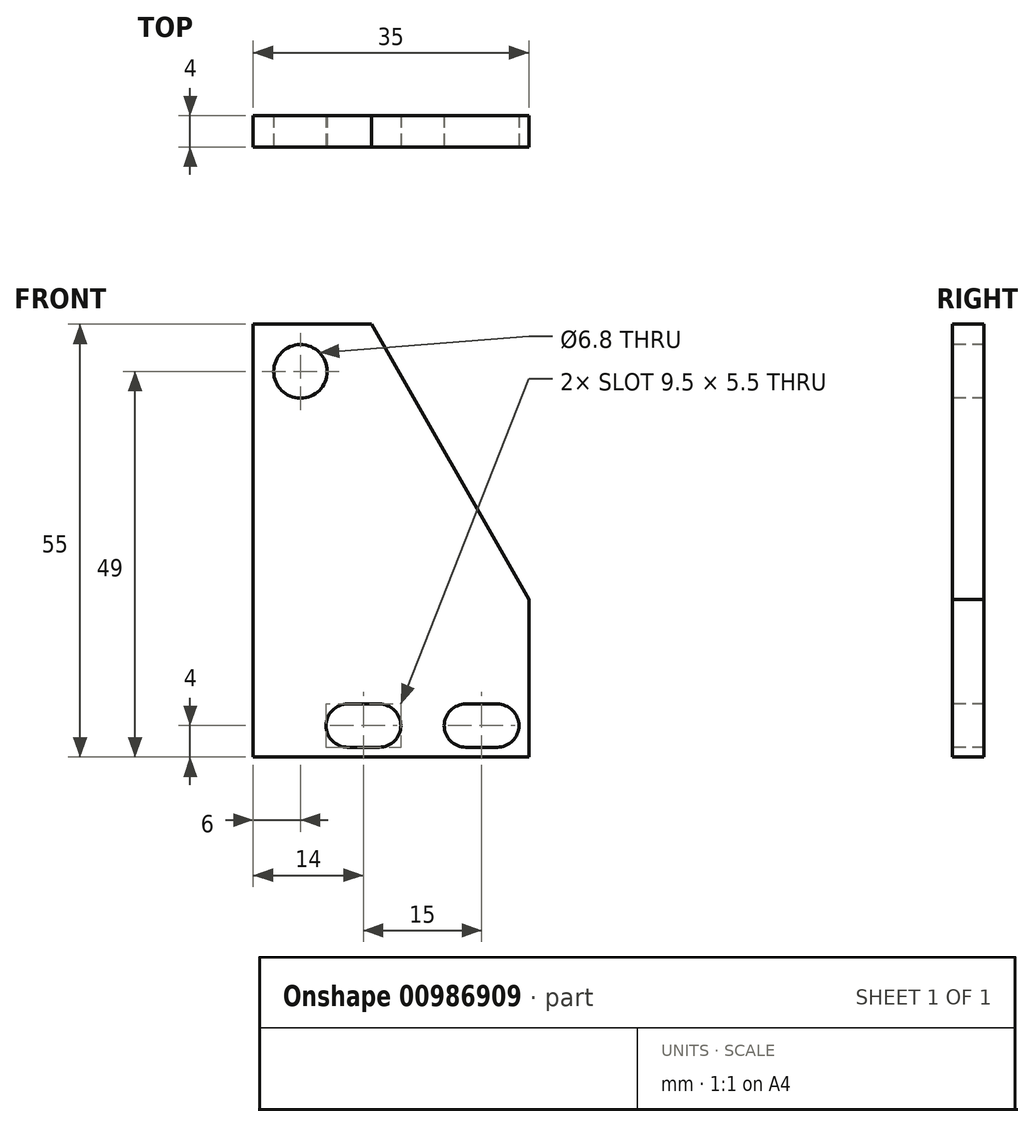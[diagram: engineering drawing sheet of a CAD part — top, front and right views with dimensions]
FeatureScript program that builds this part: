
annotation { "Feature Type Name" : "Feature", "Feature Type Description" : "" }
export const myFeature = defineFeature(function(context is Context, id is Id, definition is map)
    precondition{}
    {
        {
            var Q0;
            Q0=qCreatedBy(makeId("Front.planeOp"),FACE);
            var sketch = newSketch(context, id + "F0", { "sketchPlane" : qUnion([Q0])});
            skLineSegment(sketch, "E0", {"start": v(0, 0) * mm, "end": v(35, 0) * mm});
            skLineSegment(sketch, "E1", {"start": v(35, 0) * mm, "end": v(35, 20) * mm});
            skLineSegment(sketch, "E2", {"start": v(35, 20) * mm, "end": v(15, 55) * mm});
            skLineSegment(sketch, "E3", {"start": v(15, 55) * mm, "end": v(0, 55) * mm});
            skLineSegment(sketch, "E4", {"start": v(0, 55) * mm, "end": v(0, 0) * mm});
            skSolve(sketch);
        }
        {
            var Q0;
            Q0=makeQuery(id+"F0.imprint","IMPRINT",FACE,{"disambiguationData":[TD([[makeQuery(id+"F0.imprint","IMPRINT",EDGE,{"derivedFrom":sQuery(id+"F0.wireOp",EDGE,"E0")}),1.0]])]});
            extrude(context, id + "F1", {"entities" : qUnion([Q0]), "depth" : 4 * mm, "offsetDistance" : 25 * mm});
        }
        {
            var Q0;
            Q0=makeQuery(id+"F1.opExtrude","CAP_FACE",FACE,{"disambiguationData":[OSD([sQuery(id+"F0.wireOp",EDGE,"E0"),sQuery(id+"F0.wireOp",EDGE,"E1"),sQuery(id+"F0.wireOp",EDGE,"E2"),sQuery(id+"F0.wireOp",EDGE,"E3"),sQuery(id+"F0.wireOp",EDGE,"E4")])],"isStart":false});
            var sketch = newSketch(context, id + "F2", { "sketchPlane" : qUnion([Q0])});
            skPoint(sketch, "E5", {"position": v(6, 49) * mm});
            skPoint(sketch, "E6", {"position": v(31, 4) * mm});
            skPoint(sketch, "E7", {"position": v(16, 4) * mm});
            skPoint(sketch, "E8", {"position": v(27, 4) * mm});
            skPoint(sketch, "E9", {"position": v(12, 4) * mm});
            skCircle(sketch, "E10", {"center": v(31, 4) * mm, "radius": 2.75 * mm});
            skCircle(sketch, "E11", {"center": v(27, 4) * mm, "radius": 2.75 * mm});
            skCircle(sketch, "E12", {"center": v(16, 4) * mm, "radius": 2.75 * mm});
            skCircle(sketch, "E13", {"center": v(12, 4) * mm, "radius": 2.75 * mm});
            skLineSegment(sketch, "E14", {"start": v(12, 6.75) * mm, "end": v(16, 6.75) * mm});
            skLineSegment(sketch, "E15", {"start": v(12, 1.25) * mm, "end": v(16, 1.25) * mm});
            skLineSegment(sketch, "E16", {"start": v(27, 6.75) * mm, "end": v(31, 6.75) * mm});
            skLineSegment(sketch, "E17", {"start": v(27, 1.25) * mm, "end": v(31, 1.25) * mm});
            skSolve(sketch);
        }
        {
            var Q0;
            Q0 = qSketchRegion(id + "F2", true);
            var Q1;
            {var subQ0=sQuery(id+"F2.wireOp",EDGE,"E13");var subQ1=sQuery(id+"F2.wireOp",EDGE,"E12");var subQ2=makeQuery(id+"F2.imprint","INTERSECT",VERTEX,{"disambiguationData":[OD(0.0)],"derivedFrom":[subQ1,subQ0]});Q1=makeQuery(id+"F2.imprint","IMPRINT",FACE,{"disambiguationData":[TD([[makeQuery(id+"F2.imprint","IMPRINT",EDGE,{"disambiguationData":[TD([[subQ2,-1.0]])],"derivedFrom":subQ1}),1.0]])]});}
            var Q2;
            {var subQ0=sQuery(id+"F2.wireOp",EDGE,"E11");var subQ1=sQuery(id+"F2.wireOp",EDGE,"E10");var subQ2=makeQuery(id+"F2.imprint","INTERSECT",VERTEX,{"disambiguationData":[OD(0.0)],"derivedFrom":[subQ1,subQ0]});Q2=makeQuery(id+"F2.imprint","IMPRINT",FACE,{"disambiguationData":[TD([[makeQuery(id+"F2.imprint","IMPRINT",EDGE,{"disambiguationData":[TD([[subQ2,-1.0]])],"derivedFrom":subQ1}),1.0]])]});}
            extrude(context, id + "F3", {"entities" : qUnion([Q0, Q1, Q2]), "operationType" : NewBodyOperationType.REMOVE, "oppositeDirection" : true, "depth" : 25 * mm, "offsetDistance" : 25 * mm});
        }
        {
            var Q0;
            Q0=sQuery(id+"F2.wireOp",VERTEX,"E5");
            var Q1;
            Q1=makeQuery(id+"F1.opExtrude","SWEPT_BODY",BODY,{"disambiguationData":[OSD([sQuery(id+"F0.wireOp",EDGE,"E0"),sQuery(id+"F0.wireOp",EDGE,"E1"),sQuery(id+"F0.wireOp",EDGE,"E2"),sQuery(id+"F0.wireOp",EDGE,"E3"),sQuery(id+"F0.wireOp",EDGE,"E4")])]});
            hole(context, id + "F4", {"style" : HoleStyle.SIMPLE, "endStyle" : HoleEndStyle.BLIND, "standardTappedOrClearance" : lookupTablePath({ "standard" : "ISO", "engagement" : "75%", "pitch" : "1.25 mm", "size" : "M8", "type" : "Tapped" }), "standardBlindInLast" : lookupTablePath({ "standard" : "ISO", "fit" : "Normal", "engagement" : "75%", "pitch" : "1.25 mm", "size" : "M8", "type" : "Clearance & tapped" }), "holeDiameter" : 6.8 * mm, "majorDiameter" : 8 * mm, "showTappedDepth" : true, "holeDepth" : 15.35 * mm, "isTappedThrough" : true, "tappedDepth" : 11.6 * mm, "tapClearance" : 3, "startFromSketch" : true, "locations" : qUnion([Q0]), "scope" : qUnion([Q1])});
        }
    });
